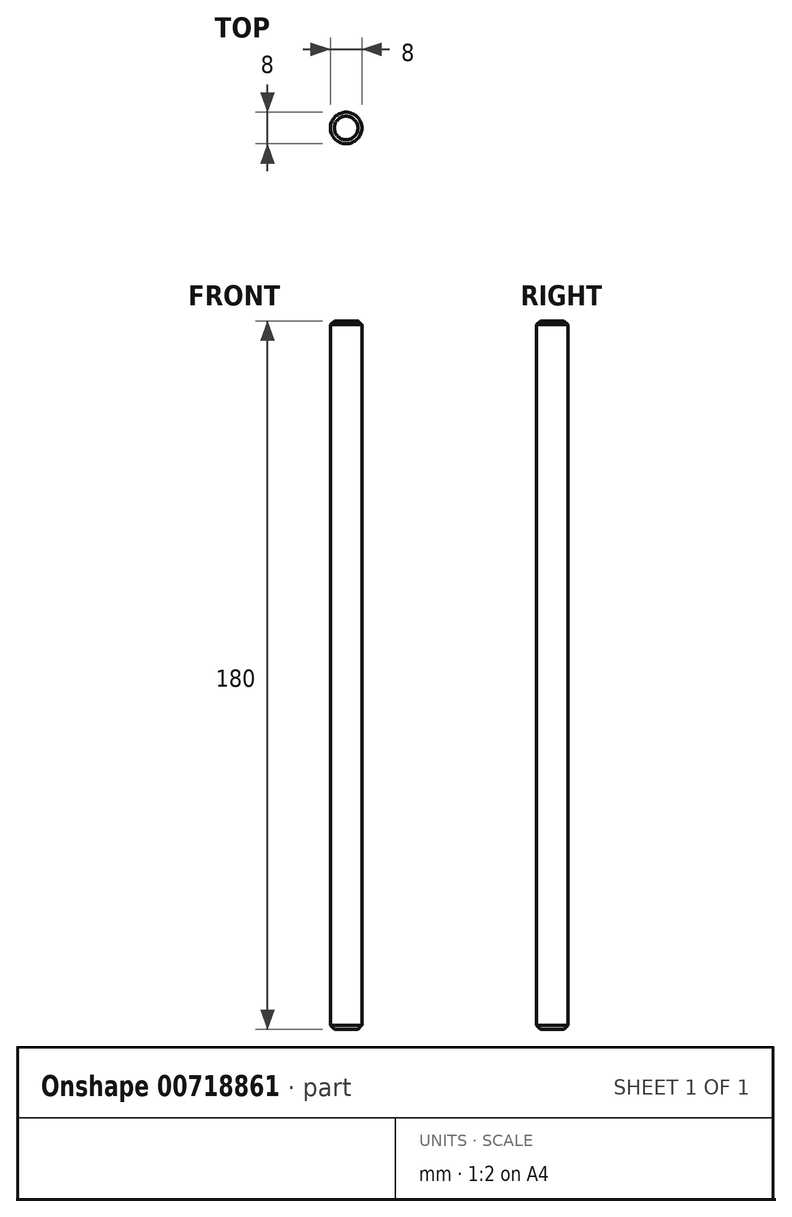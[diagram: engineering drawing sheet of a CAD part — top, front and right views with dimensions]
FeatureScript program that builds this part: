
annotation { "Feature Type Name" : "Feature", "Feature Type Description" : "" }
export const myFeature = defineFeature(function(context is Context, id is Id, definition is map)
    precondition{}
    {
        {
            var Q0;
            Q0=qCreatedBy(makeId("Top.planeOp"),FACE);
            var sketch = newSketch(context, id + "F0", { "sketchPlane" : qUnion([Q0])});
            skCircle(sketch, "E0", {"center": v(0, 0) * mm, "radius": 4 * mm});
            skSolve(sketch);
        }
        {
            var Q0;
            Q0=makeQuery(id+"F0.imprint","IMPRINT",FACE,{"disambiguationData":[TD([[makeQuery(id+"F0.imprint","IMPRINT",EDGE,{"derivedFrom":sQuery(id+"F0.wireOp",EDGE,"E0")}),1.0]])]});
            extrude(context, id + "F1", {"entities" : qUnion([Q0]), "oppositeDirection" : true, "depth" : 180 * mm, "offsetDistance" : 25 * mm});
        }
        {
            var Q0;
            Q0=makeQuery(id+"F1.opExtrude","CAP_EDGE",EDGE,{"disambiguationData":[OSD([sQuery(id+"F0.wireOp",EDGE,"E0")])],"isStart":true});
            var Q1;
            Q1=makeQuery(id+"F1.opExtrude","CAP_EDGE",EDGE,{"disambiguationData":[OSD([sQuery(id+"F0.wireOp",EDGE,"E0")])],"isStart":false});
            chamfer(context, id + "F2", {"entities" : qUnion([Q0, Q1]), "width" : 1 * mm, "tangentPropagation" : true});
        }
    });
